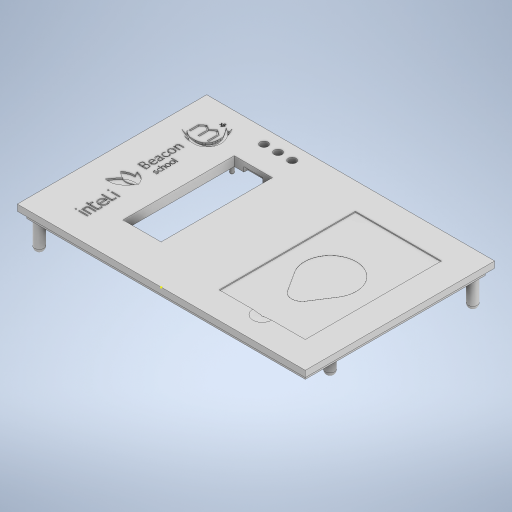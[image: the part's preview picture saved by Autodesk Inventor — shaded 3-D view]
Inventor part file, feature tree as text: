
AUTODESK INVENTOR PART (.ipt)
format: ipt  version: 2023 (Build 270158000, 158)  size: 2,886,144 bytes
history: native  units: mm
features: extrude x27, sketch x12, other x4, fillet x2
ambient origin geometry x8: Origin, YZ Plane, XZ Plane, XY Plane, X Axis, Y Axis, Z Axis, Center Point
bodies: Body1 (feature_tree)
feature tree (45):
  other  "Sólido1"
  sketch  "Esboço1"  dims[d0=184.0mm d1=121.0mm]
  extrude  "Base"  Depth=121.0mm
  extrude  "Área do Cartão"  Depth=55.0mm
  extrude  "Área da Tag"  Depth=13.0mm
  extrude  "Suporte Cartão"  Depth=71.15mm
  extrude  "Logo INTELI"  Depth=8.0mm TaperAngle=0.0deg
  extrude  "Logo BEACON"  Depth=12.0mm
  extrude  "Logo IOBEE 1"  Depth=1.0mm TaperAngle=0.0deg
  extrude  "Logo IOBEE 2"  Depth=1.0mm TaperAngle=0.0deg
  extrude  "Logo IOBEE 3"  Depth=1.0mm TaperAngle=0.0deg
  other  "Perfil LCD"
  extrude  "LCD Pinos de trás"  Depth=79.9mm
  extrude  "LCD Chaveta de trás"  Depth=40.0mm
  extrude  "LCD Alocamento"  Depth=6.0mm TaperAngle=0.0deg
  extrude  "LCD Pinos Guia"  Depth=6.0mm
  extrude  "Rasgo de Encaixe"  Depth=6.0mm
  other  "Perfil ESP32"
  extrude  "Alocamento ESP32"  Depth=5.0mm TaperAngle=0.0deg
  extrude  "ESP32 Wi-Fi"  Depth=2.0mm TaperAngle=0.0deg
  extrude  "Rasgo Protoboard"  Depth=7.0mm TaperAngle=0.0deg
  extrude  "RFID"  Depth=4.0mm TaperAngle=0.0deg
  extrude  "RFID Cabeamento"  Depth=19.0mm
  extrude  "Furo Leds"  Depth=28.0mm
  extrude  "Rasgo Fios"  Depth=8.0mm
  other  "Perfil Leds GND"
  extrude  "GND Leds"  Depth=5.0mm TaperAngle=0.0deg
  extrude  "GND Leds 2"  Depth=3.0mm TaperAngle=0.0deg
  extrude  "Fios GND"  Depth=4.5mm
  extrude  "Rasgo RFID-ESP"  Depth=5.0mm TaperAngle=0.0deg
  extrude  "Pinos de Encaixe"  Depth=4.5mm
  fillet  "Arredondamento-  Pinos de Encaixe"  Radius=60.0mm
  fillet  "Arredondamento- Pinos Guia LCD"  Radius=6.0mm
  extrude  "Entrada USB-C ESP32"  Depth=4.5mm
  sketch  "Esboço30"  dims[d48=6.2mm d49=6.0mm d50=0.0mm d51=6.0mm d52=6.0mm d53=5.0mm d54=0.0mm d55=2.0mm d56=0.0mm d69=7.0mm d70=0.0mm d72=4.0mm d73=0.0mm d111=19.0mm d112=28.0mm d113=8.0mm d114=5.0mm d115=0.0mm d116=3.0mm d117=0.0mm d120=164.0mm d122=5.0mm d123=0.0mm d130=39.4mm d131=60.0mm d132=6.0mm d133=0.0mm d136=20.4mm d138=3.0mm d139=0.0mm d140=5.0mm d141=5.0mm d142=5.0mm d143=9.0mm d145=9.0mm d149=18.0mm d151=11.469816mm d152=0.0mm d153=0.0mm d158=2.0mm d159=0.0mm d162=2.0mm d163=0.0mm d166=10.0mm d167=2.8mm d168=2.0mm d169=0.0mm d170=13.0mm d171=2.0mm d172=0.0mm d173=2.0mm d174=0.0mm d177=6.0mm d180=6.0mm d183=6.0mm d184=6.0mm d185=18.0mm d186=0.0mm d191=3.0mm d196=1.0mm d197=60.0mm d199=0.0mm d200=0.0mm d201=2.5mm d202=75.9mm d203=32.05mm d209=178.0mm d210=115.0mm d211=4.5mm d57=0.5mm d58=0.872665mm d59=0.5mm d60=0.872665mm d86=0.872665mm d87=0.872665mm d124=0.5mm d125=0.872665mm d175=0.5mm d176=0.872665mm]
  sketch  "Esboço3"  dims[d2=55.0mm d3=87.0mm]
  sketch  "Esboço4"  dims[d5=17.0mm d8=13.0mm]
  sketch  "Esboço12"  dims[d9=24.36mm d10=71.15mm]
  sketch  "Esboço18"  dims[d24=8.0mm d25=0.0mm d26=0.6mm d27=0.0mm]
  sketch  "Esboço19"  dims[d28=0.7mm d29=0.0mm d30=12.0mm]
  sketch  "Esboço21"  dims[d31=0.6mm d32=-14.660766mm d33=1.0mm d34=0.0mm]
  sketch  "Esboço24"  dims[d35=1.0mm d36=0.0mm d37=0.5mm d38=0.0mm]
  sketch  "Esboço25"  dims[d39=1.0mm d40=0.0mm d41=1.2mm d42=0.0mm]
  sketch  "Esboço26"  dims[d43=36.05mm d44=79.9mm]
  sketch  "Esboço29"  dims[d45=4.0mm d47=40.0mm]
